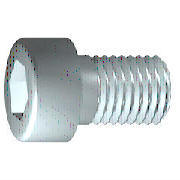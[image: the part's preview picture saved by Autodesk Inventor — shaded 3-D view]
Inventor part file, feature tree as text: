
AUTODESK INVENTOR PART (.ipt)
format: ipt  version: 2020 (Build 240168000, 168)  size: 201,728 bytes
history: native  units: mm (DEFAULTED — no unit token found)
features: sketch x2, extrude x1, plane x1, fillet x1
ambient origin geometry x7: Origin, YZ Plane, XY Plane, X Axis, Y Axis, Z Axis, Center Point
bodies: Solid1 (feature_tree), Body (feature_tree)
feature tree (5):
  extrude  "Slot"  Depth=3.0mm
  plane  "Work Plane1"
  fillet  "Fillet2"  Radius=3.0mm
  sketch  "Sketch1"  dims[d1=3.75mm d2=0.306825mm d3=3.0mm]
  sketch  "Sketch2"  dims[d4=1.3mm d5=60.0deg d6=3.0mm d7=3.0mm d8=2.886751mm d9=5.5mm d10=90.0deg d11=10.0mm d12=0.0mm d13=3.75mm d14=0.0mm d15=0.306725mm d16=0.306725mm d17=0.3mm d19=0.0mm d26=5.0mm d27=45.0deg d28=0.0mm d29=0.0mm d30=0.1mm]
